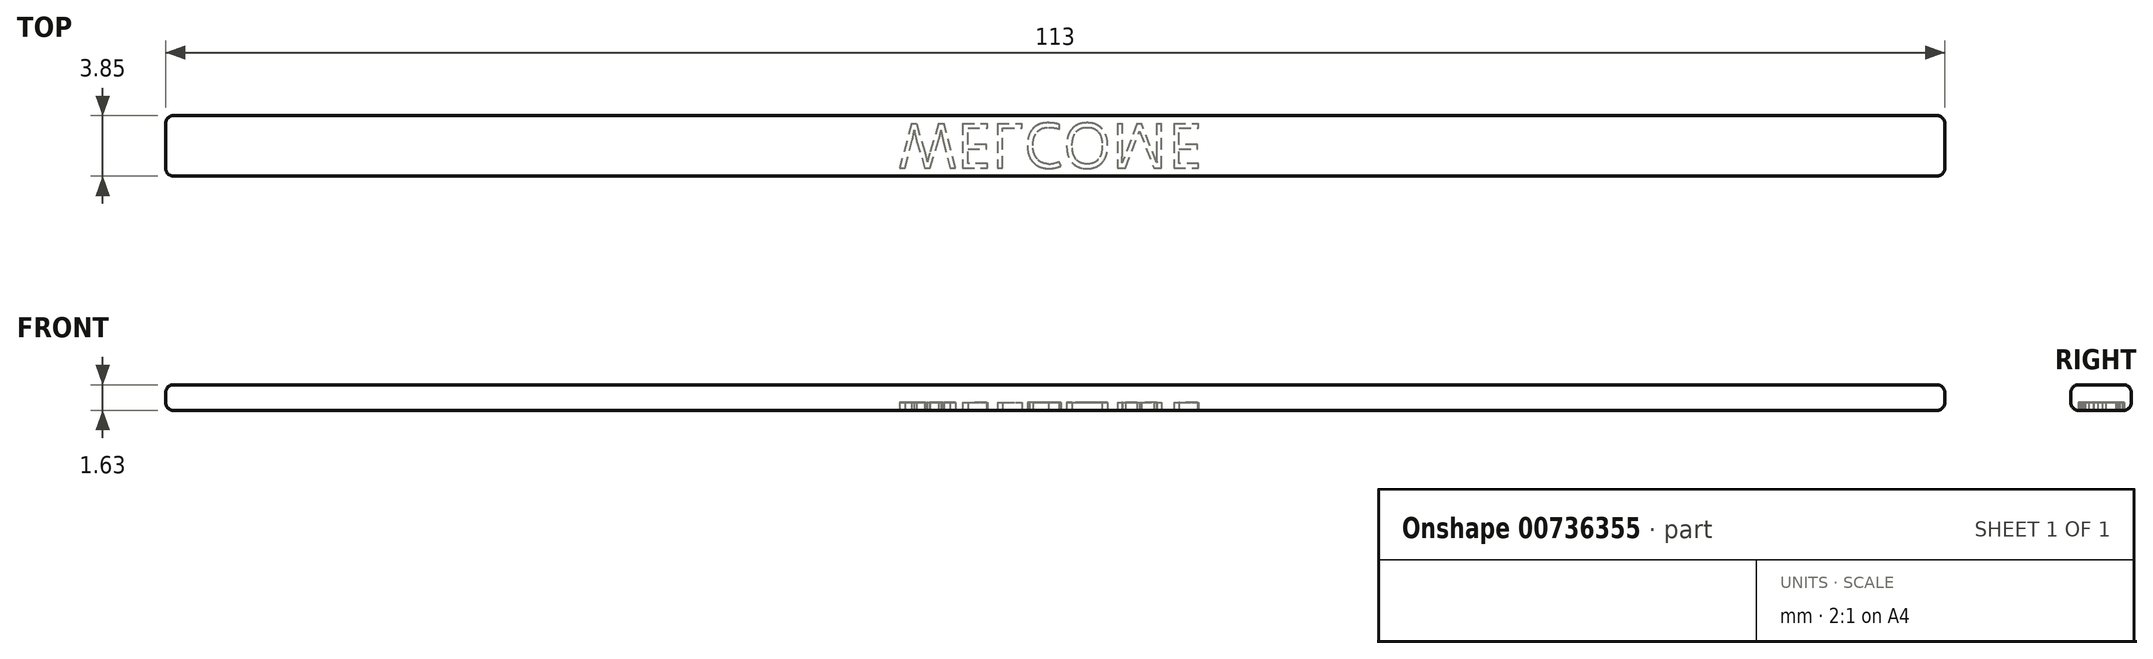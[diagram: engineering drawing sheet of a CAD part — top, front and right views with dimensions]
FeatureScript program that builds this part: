
annotation { "Feature Type Name" : "Feature", "Feature Type Description" : "" }
export const myFeature = defineFeature(function(context is Context, id is Id, definition is map)
    precondition{}
    {
        {
            var Q0;
            Q0=qCreatedBy(makeId("Top.planeOp"),FACE);
            var sketch = newSketch(context, id + "F0", { "sketchPlane" : qUnion([Q0])});
            skLineSegment(sketch, "E0", {"start": v(-56.22, 0) * mm, "end": v(-56.22, 3.85) * mm});
            skLineSegment(sketch, "E1", {"start": v(-56.22, 3.85) * mm, "end": v(56.78, 3.85) * mm});
            skLineSegment(sketch, "E2", {"start": v(56.78, 3.85) * mm, "end": v(56.78, 0) * mm});
            skLineSegment(sketch, "E3", {"start": v(56.78, 0) * mm, "end": v(-56.22, 0) * mm});
            skSolve(sketch);
        }
        {
            var Q0;
            Q0 = qSketchRegion(id + "F0", true);
            extrude(context, id + "F1", {"entities" : qUnion([Q0]), "depth" : 1.63 * mm, "offsetDistance" : 25 * mm});
        }
        {
            var Q0;
            Q0=makeQuery(id+"F1.opExtrude","CAP_FACE",FACE,{"disambiguationData":[OSD([sQuery(id+"F0.wireOp",EDGE,"E0"),sQuery(id+"F0.wireOp",EDGE,"E1"),sQuery(id+"F0.wireOp",EDGE,"E2"),sQuery(id+"F0.wireOp",EDGE,"E3")])],"isStart":false});
            var Q1;
            Q1=makeQuery(id+"F1.opExtrude","CAP_FACE",FACE,{"disambiguationData":[OSD([sQuery(id+"F0.wireOp",EDGE,"E0"),sQuery(id+"F0.wireOp",EDGE,"E1"),sQuery(id+"F0.wireOp",EDGE,"E2"),sQuery(id+"F0.wireOp",EDGE,"E3")])],"isStart":true});
            fillet(context, id + "F2", {"entities" : qUnion([Q0, Q1]), "radius" : 0.5 * mm, "tangentPropagation" : true, "allowEdgeOverflow" : false});
        }
        {
            var Q0;
            Q0=makeQuery(id+"F1.opExtrude","SWEPT_FACE",FACE,{"disambiguationData":[OSD([sQuery(id+"F0.wireOp",EDGE,"E0")])]});
            var Q1;
            Q1=makeQuery(id+"F1.opExtrude","SWEPT_FACE",FACE,{"disambiguationData":[OSD([sQuery(id+"F0.wireOp",EDGE,"E2")])]});
            fillet(context, id + "F3", {"entities" : qUnion([Q0, Q1]), "radius" : 0.5 * mm, "tangentPropagation" : true, "allowEdgeOverflow" : false});
        }
        {
            var Q0;
            Q0=makeQuery(id+"F1.opExtrude","CAP_FACE",FACE,{"disambiguationData":[OSD([sQuery(id+"F0.wireOp",EDGE,"E0"),sQuery(id+"F0.wireOp",EDGE,"E1"),sQuery(id+"F0.wireOp",EDGE,"E2"),sQuery(id+"F0.wireOp",EDGE,"E3")])],"isStart":true});
            var sketch = newSketch(context, id + "F4", { "sketchPlane" : qUnion([Q0])});
            skText(sketch, "E4", { "text": "WELCOME", "fontName": "OpenSans-Regular.ttf"});
            const initialGuessF4  = {"E4": [-0.00965, -0.00335, 1, 0, 0.00285]};
            skSetInitialGuess(sketch, initialGuessF4);
            skSolve(sketch);
        }
        {
            var Q0;
            Q0 = qSketchRegion(id + "F4", true);
            extrude(context, id + "F5", {"entities" : qUnion([Q0]), "operationType" : NewBodyOperationType.REMOVE, "oppositeDirection" : true, "depth" : 0.5 * mm, "offsetDistance" : 25 * mm});
        }
    });
